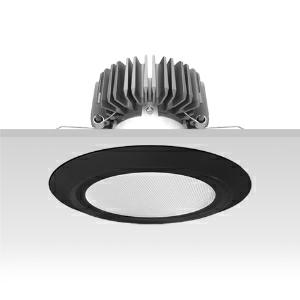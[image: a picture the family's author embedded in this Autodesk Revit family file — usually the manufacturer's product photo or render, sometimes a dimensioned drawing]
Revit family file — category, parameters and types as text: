
# Revit family: 3f_filippi_-_3f_reno_bianco_ampio_3f_filippi_-_30641_a01038_-_3f_reno_200_wh_4000-930_wide___vs_bk_9779
name_source: partatom
category: Lighting Fixtures
units: mm (PartAtom-declared; Revit-internal decimal feet)

## family parameters
Cut with Voids When Loaded = No
Host = Face
Light Source = No
Part Type = Normal
Room Calculation Point = No
Round Connector Dimension = Use Diameter
Shared = No

## types (1)
- 3F Filippi - 3F Reno Bianco Ampio (1 x LED, 2801 lm, 43 W, 3000 K)
    Apparent Load = 43 VA
    Approval mark = CE
    CIE Flux Codes = 75 94 99 100 100
    Color Rendering = 90
    Color Temperature = 3000 K
    Control Gear = Electronic ballast
    Default Elevation = 1800 mm
    Description = ILLUMINOTECHNICAL
Luminous efficiency 100% (DLOR 100%, ULOR 0%).
Initial luminous flux of the luminaire 2801 lm.
Direct symmetric wide distribution.
Installation Interdistance Transv.D = 1.16 x hu - Long.D = 1.14 x hu.
Tabular UGR (CIE 117 - 4H-8H; S=0.25H; 70/50/20): RUG 22.1 - 22.
Beam angle: 74° - 74°.
Luminous efficacy 65 lm/W.
Lifetime (L90/B10): 30000 h. (tq+25°C)
Lifetime (L85/B10): 50000 h. (tq+25°C)
Lifetime (L70/B10): 80000 h. (tq+25°C)
Sudden decreased luminous flux after 50000 hours: 0% (C0).
Photobiological safety in compliance with IEC/TR 62778: RG1 low risk, (IEC 62471).
In compliance with IEC/EN 62722-2-1 - IEC/EN 62717 standards.

SOURCE
Compact LED module 4000/930.
Energy efficiency class (UE 2019/2020 - UE 2019/2015): F.
CIE 13.3 Colour rendering index: CRI >90 (R9 >50%).
IES TM-30 Fidelity Index: Rf = 92 Rg = 101.
CCT nominal colour temperature 3000 K.
Colour initial tolerance (MacAdam): SDCM 3.
Zhaga Book 3 compliant.

MECHANICAL
Passive heat dissipator in die-casting aluminium, oversized, for optimum thermal management of the LED module.
Parabolic element with graduated/concentric rings in white polycarbonate.
Transparent external lens with glossy and satin differentiated surfaces, with a cooling and anti-insect system in methacrylate (PMMA).
Fastening spring clips in stainless steel.
Dimensions: diameter 226 mm, height 146 mm. Weight 1.775 kg.
IP44 protection degree for exposed part, IP20 for recessed part.
Mechanical strength to impacts IK06 (1 joule).
Glow-wire test resistance 650°C.

ELECTRICAL
Wiring on a separate unit.
Halogen Free electronic wiring 230V-50/60Hz, power factor 0.95, THD <25%, constant output current, SELV, class II, 1 driver.
Power of the luminaire 43 W.
ENEC - CE.
SAFE FLICKER: PstLM=<1 and SVM=<0.4 (IEC TR 61547-1 and IEC TR 63158), to ensure a more comfortable and safe light.
Luminaire compliant with EN 60598-2-22 for power supply from a centralised emergency system CPSS (Central Power Supply System), not incorporated in the luminaire - high risk areas excluded. The default power and flux are 100% in AC and 100% in DC.
Ambient temperature from 0°C to +25°C.
Temperature class T6 max 85°C.
Relative humidity UR: <85%.

INSTALLATION
Pull-up recessed fitting.
False ceiling carving: 200 mm.
All accessories dedicated to this product are available on the Catalog and on our website www.3F-Filippi.com.

ACCESSORIES
A01038 - Anti-glare microprismatic VS moulded glass, tempered, not flammable, locked and in line with the trim, in black polycarbonate.

APPLICATIONS
Environments: architectural, commercial, exhibition areas, transit areas, corridors, shops, display windows, service areas.
In false ceilings with narrow voids.

WARNING
Luminaire designed for disposal/recycling at end-of-life.
Replaceable (LED only) light source by a professional. Replaceable control gear by a professional.
    Height = 0 mm  [stored 0 ft]
    Lamp = 1 x LED
    Lamp Light Flux = 2801 lm
    Lamp Power = 43 W
    Lamp count = 1
    Length = 226 mm
    Lifetime = 50000 h
    Luminous efficacy = 65 lm/W
    Manufacturer = 3F Filippi
    ModVariant = No
    Model = 3F Filippi - 30641+A01038 - 3F Reno 200 WH 4000-930 WIDE + VS BK
    Mounting Place = Ceiling
    Mounting Type = Recessed
    Number of Poles = 1
    OnlyDefault = Yes
    Power Factor = 1
    Product Name = 3F Filippi - 3F Reno Bianco Ampio
    Product group = recessed luminaire
    ProductGroupID = 4
    Protection Class = Protection class II
    Protection Degree = IP 20
    RLX_Detail_Level = 1
    RLX_Emergency_Light_Flux = 0 lm
    RLX_Emergency_Type = 0
    RLX_Emergency_Type_DB = No
    RlxData = <blob elided: 97857 chars, md5=d2da64c8>
    Socket = socket
    Standby Power = 0 W
    System Light Flux = 2801 lm
    System Power = 43 W
    Type Comments = Product without accessories
    Type Image = 3ffilippi_3f_reno_200_bk_vs_smp.jpg
    URL = http://relux.com
    VarID = ---
    Voltage = 0 V
    Weight = 0.00 kg
    Width = 0 mm  [stored 0 ft]

note: [stored X ft] marks values corroborated as IEEE doubles in the binary element streams (Revit-internal decimal feet)

## geometry (parser evidence)
native form markers: Blend x4, Sweep x8
no freeform markers — native parametric forms only
